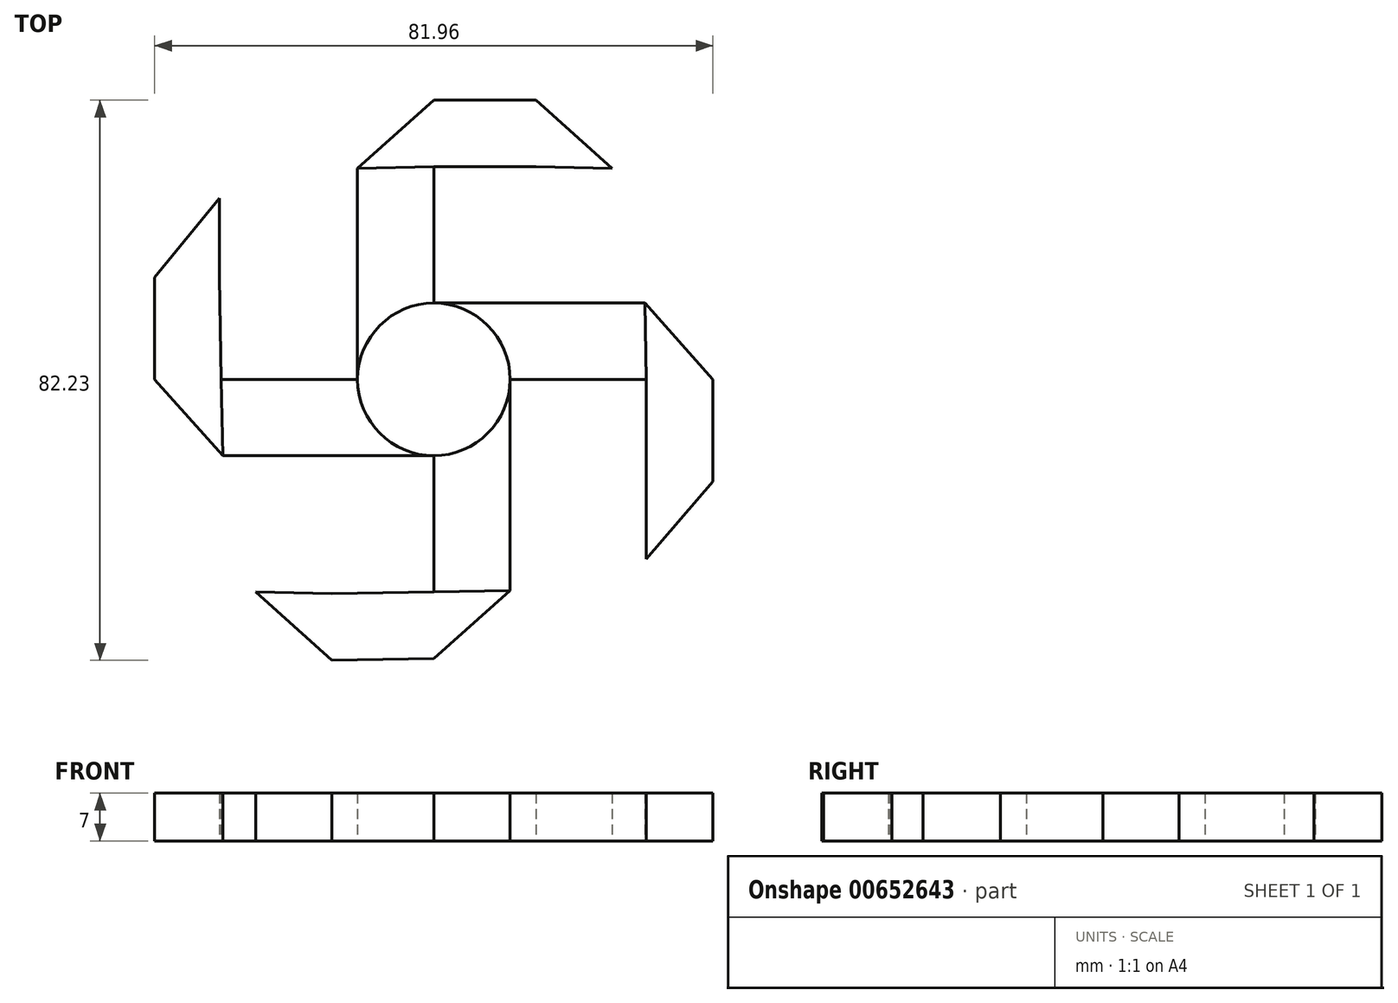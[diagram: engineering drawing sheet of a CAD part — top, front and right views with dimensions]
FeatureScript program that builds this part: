
annotation { "Feature Type Name" : "Feature", "Feature Type Description" : "" }
export const myFeature = defineFeature(function(context is Context, id is Id, definition is map)
    precondition{}
    {
        {
            var Q0;
            Q0=qCreatedBy(makeId("Top.planeOp"),FACE);
            var sketch = newSketch(context, id + "F0", { "sketchPlane" : qUnion([Q0])});
            skCircle(sketch, "E0", {"center": v(0, 0) * mm, "radius": 11.2 * mm});
            skLineSegment(sketch, "E1", {"start": v(0, 11.2) * mm, "end": v(0, 31.2) * mm});
            skLineSegment(sketch, "E2", {"start": v(11.2, 0) * mm, "end": v(31.2, 0) * mm});
            skLineSegment(sketch, "E3", {"start": v(0, -11.2) * mm, "end": v(0, -31.2) * mm});
            skLineSegment(sketch, "E4", {"start": v(-11.2, 0) * mm, "end": v(-31.2, 0) * mm});
            skLineSegment(sketch, "E5", {"start": v(-11.2, 0) * mm, "end": v(-11.2, 31) * mm});
            skLineSegment(sketch, "E6", {"start": v(0, 11.2) * mm, "end": v(31, 11.2) * mm});
            skLineSegment(sketch, "E7", {"start": v(11.2, 0) * mm, "end": v(11.2, -31) * mm});
            skLineSegment(sketch, "E8", {"start": v(0, -11.2) * mm, "end": v(-31, -11.2) * mm});
            skLineSegment(sketch, "E9", {"start": v(-11.2, 31) * mm, "end": v(0, 31.2) * mm});
            skLineSegment(sketch, "E10", {"start": v(31, 11.2) * mm, "end": v(31.2, 0) * mm});
            skLineSegment(sketch, "E11", {"start": v(11.2, -31) * mm, "end": v(0, -31.2) * mm});
            skLineSegment(sketch, "E12", {"start": v(-31, -11.2) * mm, "end": v(-31.2, 0) * mm});
            skLineSegment(sketch, "E13", {"start": v(-11.2, 31) * mm, "end": v(0, 40.98) * mm});
            skPoint(sketch, "E13.endSnap0", {"position": v(0, 21.2) * mm});
            skLineSegment(sketch, "E14", {"start": v(0, 31.2) * mm, "end": v(15, 31.2) * mm});
            skLineSegment(sketch, "E15", {"start": v(0, 40.98) * mm, "end": v(15, 40.98) * mm});
            skLineSegment(sketch, "E16", {"start": v(15, 40.98) * mm, "end": v(26.2, 31) * mm});
            skLineSegment(sketch, "E17", {"start": v(15, 31.2) * mm, "end": v(26.2, 31) * mm});
            skLineSegment(sketch, "E18", {"start": v(31, 11.2) * mm, "end": v(40.98, 0) * mm});
            skLineSegment(sketch, "E19", {"start": v(31.2, 0) * mm, "end": v(31.2, -15) * mm});
            skLineSegment(sketch, "E20", {"start": v(40.98, 0) * mm, "end": v(40.98, -15) * mm});
            skLineSegment(sketch, "E21", {"start": v(40.98, -15) * mm, "end": v(31.2, -26.38) * mm});
            skLineSegment(sketch, "E22", {"start": v(31.2, -15) * mm, "end": v(31.2, -26.38) * mm});
            skLineSegment(sketch, "E23", {"start": v(0, -31.2) * mm, "end": v(-15, -31.47) * mm});
            skLineSegment(sketch, "E24", {"start": v(11.2, -31) * mm, "end": v(0, -40.98) * mm});
            skLineSegment(sketch, "E25", {"start": v(0, -40.98) * mm, "end": v(-15, -41.25) * mm});
            skLineSegment(sketch, "E26", {"start": v(-15, -41.25) * mm, "end": v(-26.14, -31.2) * mm});
            skLineSegment(sketch, "E27", {"start": v(-15, -31.47) * mm, "end": v(-26.14, -31.2) * mm});
            skLineSegment(sketch, "E28", {"start": v(-31.2, 0) * mm, "end": v(-31.47, 15) * mm});
            skLineSegment(sketch, "E29", {"start": v(-31, -11.2) * mm, "end": v(-40.98, 0) * mm});
            skLineSegment(sketch, "E30", {"start": v(-40.98, 0) * mm, "end": v(-40.98, 15) * mm});
            skLineSegment(sketch, "E31", {"start": v(-40.98, 15) * mm, "end": v(-31.47, 26.6) * mm});
            skLineSegment(sketch, "E32", {"start": v(-31.47, 26.6) * mm, "end": v(-31.47, 15) * mm});
            skSolve(sketch);
        }
        {
            var Q0;
            {var subQ2=sQuery(id+"F0.wireOp",EDGE,"E2");Q0=makeQuery(id+"F0.imprint","IMPRINT",FACE,{"disambiguationData":[TD([[makeQuery(id+"F0.imprint","IMPRINT",EDGE,{"derivedFrom":subQ2}),1.0]])]});}
            var Q1;
            {var subQ2=sQuery(id+"F0.wireOp",EDGE,"E3");Q1=makeQuery(id+"F0.imprint","IMPRINT",FACE,{"disambiguationData":[TD([[makeQuery(id+"F0.imprint","IMPRINT",EDGE,{"derivedFrom":subQ2}),1.0]])]});}
            var Q2;
            {var subQ2=sQuery(id+"F0.wireOp",EDGE,"E4");Q2=makeQuery(id+"F0.imprint","IMPRINT",FACE,{"disambiguationData":[TD([[makeQuery(id+"F0.imprint","IMPRINT",EDGE,{"derivedFrom":subQ2}),1.0]])]});}
            var Q3;
            {var subQ0=sQuery(id+"F0.wireOp",EDGE,"E1");Q3=makeQuery(id+"F0.imprint","IMPRINT",FACE,{"disambiguationData":[TD([[makeQuery(id+"F0.imprint","IMPRINT",EDGE,{"derivedFrom":subQ0}),1.0]])]});}
            extrude(context, id + "F1", {"entities" : qUnion([Q0, Q1, Q2, Q3]), "depth" : 7 * mm, "offsetDistance" : 25 * mm});
        }
        {
            var Q0;
            Q0=makeQuery(id+"F0.imprint","IMPRINT",FACE,{"disambiguationData":[TD([[makeQuery(id+"F0.imprint","IMPRINT",EDGE,{"derivedFrom":sQuery(id+"F0.wireOp",EDGE,"E9")}),1.0]])]});
            var Q1;
            {var subQ0=sQuery(id+"F0.wireOp",EDGE,"E1");Q1=makeQuery(id+"F0.imprint","IMPRINT",FACE,{"disambiguationData":[TD([[makeQuery(id+"F0.imprint","IMPRINT",EDGE,{"derivedFrom":subQ0}),1.0]])]});}
            var Q2;
            Q2=makeQuery(id+"F0.imprint","IMPRINT",FACE,{"disambiguationData":[TD([[makeQuery(id+"F0.imprint","IMPRINT",EDGE,{"derivedFrom":sQuery(id+"F0.wireOp",EDGE,"E12")}),1.0]])]});
            var Q3;
            {var subQ2=sQuery(id+"F0.wireOp",EDGE,"E4");Q3=makeQuery(id+"F0.imprint","IMPRINT",FACE,{"disambiguationData":[TD([[makeQuery(id+"F0.imprint","IMPRINT",EDGE,{"derivedFrom":subQ2}),1.0]])]});}
            var Q4;
            {var subQ2=sQuery(id+"F0.wireOp",EDGE,"E2");Q4=makeQuery(id+"F0.imprint","IMPRINT",FACE,{"disambiguationData":[TD([[makeQuery(id+"F0.imprint","IMPRINT",EDGE,{"derivedFrom":subQ2}),1.0]])]});}
            var Q5;
            Q5=makeQuery(id+"F0.imprint","IMPRINT",FACE,{"disambiguationData":[TD([[makeQuery(id+"F0.imprint","IMPRINT",EDGE,{"derivedFrom":sQuery(id+"F0.wireOp",EDGE,"E10")}),1.0]])]});
            var Q6;
            Q6=makeQuery(id+"F0.imprint","IMPRINT",FACE,{"disambiguationData":[TD([[makeQuery(id+"F0.imprint","IMPRINT",EDGE,{"derivedFrom":sQuery(id+"F0.wireOp",EDGE,"E11")}),1.0]])]});
            var Q7;
            {var subQ2=sQuery(id+"F0.wireOp",EDGE,"E3");Q7=makeQuery(id+"F0.imprint","IMPRINT",FACE,{"disambiguationData":[TD([[makeQuery(id+"F0.imprint","IMPRINT",EDGE,{"derivedFrom":subQ2}),1.0]])]});}
            extrude(context, id + "F2", {"entities" : qUnion([Q0, Q1, Q2, Q3, Q4, Q5, Q6, Q7]), "depth" : 7 * mm, "offsetDistance" : 25 * mm});
        }
    });
